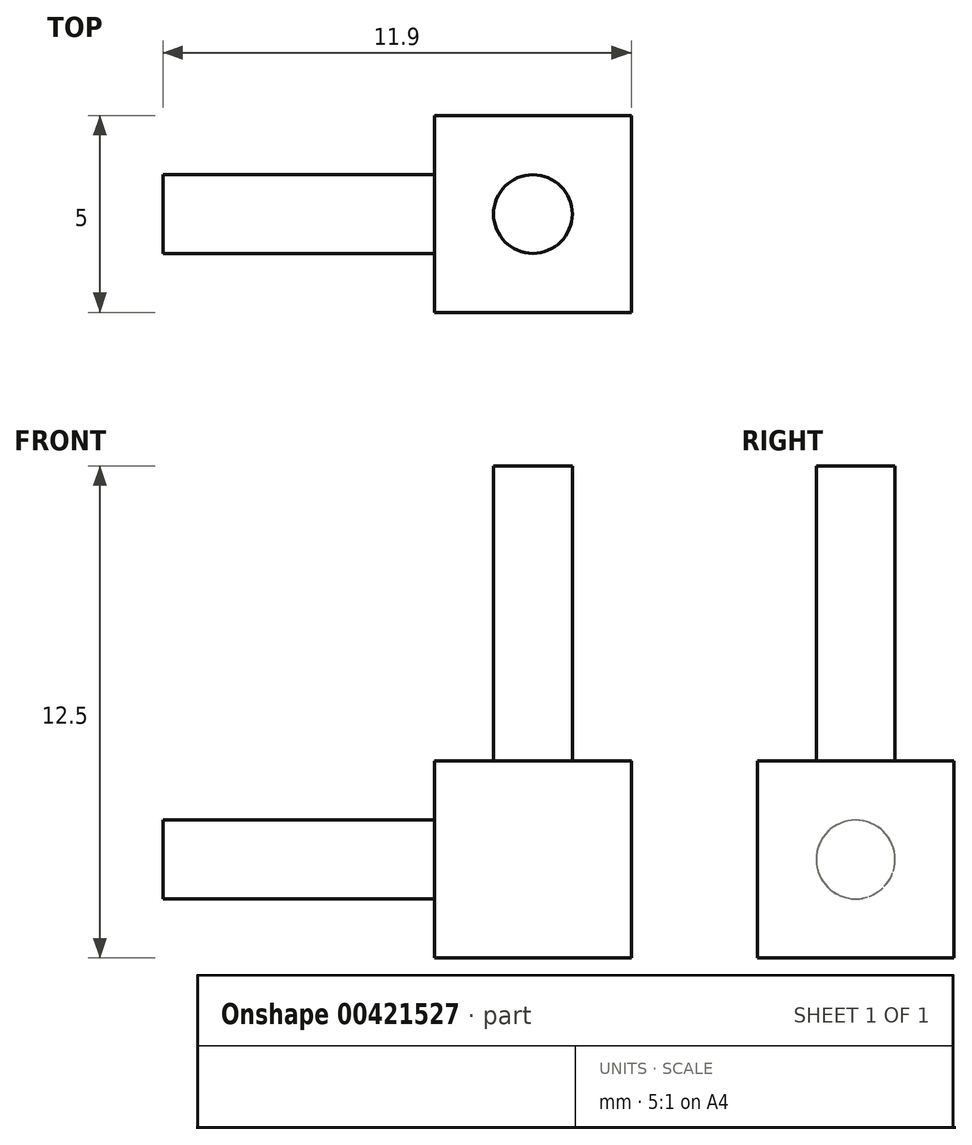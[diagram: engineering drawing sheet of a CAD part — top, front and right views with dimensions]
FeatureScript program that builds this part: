
annotation { "Feature Type Name" : "Feature", "Feature Type Description" : "" }
export const myFeature = defineFeature(function(context is Context, id is Id, definition is map)
    precondition{}
    {
        {
            var Q0;
            Q0=qCreatedBy(makeId("Front.planeOp"),FACE);
            var sketch = newSketch(context, id + "F0", { "sketchPlane" : qUnion([Q0])});
            skLineSegment(sketch, "E0.bottom", {"start": v(0, 0) * mm, "end": v(-9.4, 0) * mm});
            skLineSegment(sketch, "E0.right", {"start": v(-9.4, 0) * mm, "end": v(-9.4, -1) * mm});
            skLineSegment(sketch, "E1.top", {"start": v(0, 10) * mm, "end": v(1, 10) * mm});
            skLineSegment(sketch, "E1.left", {"start": v(0, 0) * mm, "end": v(0, 10) * mm});
            skPoint(sketch, "E2", {"position": v(1, -1) * mm});
            skLineSegment(sketch, "E3", {"start": v(1, -1) * mm, "end": v(0, 0) * mm});
            skLineSegment(sketch, "E4", {"start": v(1, -1) * mm, "end": v(-9.4, -1) * mm});
            skLineSegment(sketch, "E5", {"start": v(1, -1) * mm, "end": v(1, 10) * mm});
            skLineSegment(sketch, "E6.bottom", {"start": v(2.5, -2.5) * mm, "end": v(-2.5, -2.5) * mm});
            skLineSegment(sketch, "E6.top", {"start": v(2.5, 2.5) * mm, "end": v(-2.5, 2.5) * mm});
            skLineSegment(sketch, "E6.left", {"start": v(2.5, -2.5) * mm, "end": v(2.5, 2.5) * mm});
            skLineSegment(sketch, "E6.right", {"start": v(-2.5, -2.5) * mm, "end": v(-2.5, 2.5) * mm});
            skPoint(sketch, "E6.middle", {"position": v(0, 0) * mm});
            skSolve(sketch);
        }
        {
            var Q0;
            Q0=makeQuery(id+"F0.imprint","IMPRINT",FACE,{"disambiguationData":[TD([[makeQuery(id+"F0.imprint","IMPRINT",EDGE,{"derivedFrom":sQuery(id+"F0.wireOp",EDGE,"E0.bottom")}),1.0]])]});
            var Q1;
            Q1=sQuery(id+"F0.wireOp",EDGE,"E0.bottom");
            revolve(context, id + "F1", {"entities" : qUnion([Q0]), "axis" : qUnion([Q1]), "revolveType" : RevolveType.FULL});
        }
        {
            var Q0;
            Q0=makeQuery(id+"F0.imprint","IMPRINT",FACE,{"disambiguationData":[TD([[makeQuery(id+"F0.imprint","IMPRINT",EDGE,{"derivedFrom":sQuery(id+"F0.wireOp",EDGE,"E1.top")}),-1.0]])]});
            var Q1;
            {var subQ0=sQuery(id+"F0.wireOp",EDGE,"E3");Q1=makeQuery(id+"F0.imprint","IMPRINT",FACE,{"disambiguationData":[TD([[makeQuery(id+"F0.imprint","IMPRINT",EDGE,{"derivedFrom":subQ0}),-1.0]])]});}
            var Q2;
            Q2=sQuery(id+"F0.wireOp",EDGE,"E1.left");
            revolve(context, id + "F2", {"operationType" : NewBodyOperationType.ADD, "entities" : qUnion([Q0, Q1]), "axis" : qUnion([Q2]), "revolveType" : RevolveType.FULL});
        }
        {
            var Q0;
            {var subQ0=sQuery(id+"F0.wireOp",EDGE,"E6.bottom");Q0=makeQuery(id+"F0.imprint","IMPRINT",FACE,{"disambiguationData":[TD([[makeQuery(id+"F0.imprint","IMPRINT",EDGE,{"derivedFrom":subQ0}),-1.0]])]});}
            var Q1;
            {var subQ3=sQuery(id+"F0.wireOp",EDGE,"E6.right");var subQ5=sQuery(id+"F0.wireOp",EDGE,"E6.top");var subQ7=makeQuery(id+"F0.imprint","INTERSECT",VERTEX,{"derivedFrom":[subQ5,subQ3]});Q1=makeQuery(id+"F0.imprint","IMPRINT",FACE,{"disambiguationData":[TD([[makeQuery(id+"F0.imprint","IMPRINT",EDGE,{"disambiguationData":[TD([[subQ7,1.0]])],"derivedFrom":subQ5}),1.0]])]});}
            var Q2;
            {var subQ0=sQuery(id+"F0.wireOp",EDGE,"E3");Q2=makeQuery(id+"F0.imprint","IMPRINT",FACE,{"disambiguationData":[TD([[makeQuery(id+"F0.imprint","IMPRINT",EDGE,{"derivedFrom":subQ0}),-1.0]])]});}
            var Q3;
            {var subQ0=sQuery(id+"F0.wireOp",EDGE,"E3");Q3=makeQuery(id+"F0.imprint","IMPRINT",FACE,{"disambiguationData":[TD([[makeQuery(id+"F0.imprint","IMPRINT",EDGE,{"derivedFrom":subQ0}),1.0]])]});}
            extrude(context, id + "F3", {"entities" : qUnion([Q0, Q1, Q2, Q3]), "operationType" : NewBodyOperationType.ADD, "depth" : 5 * mm, "symmetric" : true});
        }
    });
